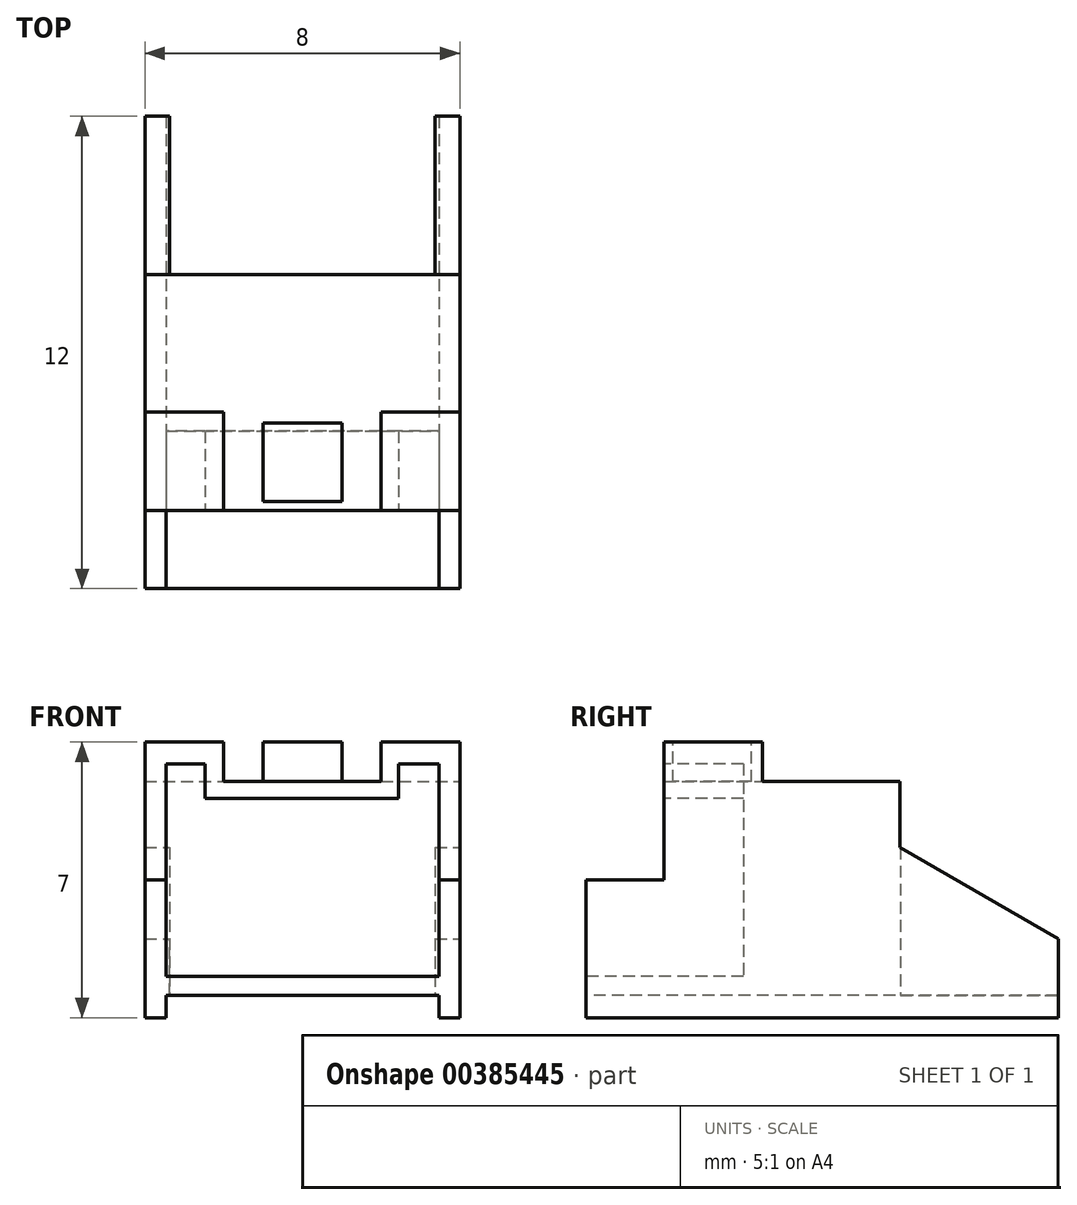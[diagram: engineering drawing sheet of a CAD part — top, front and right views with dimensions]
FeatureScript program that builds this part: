
annotation { "Feature Type Name" : "Feature", "Feature Type Description" : "" }
export const myFeature = defineFeature(function(context is Context, id is Id, definition is map)
    precondition{}
    {
        {
            var Q0;
            Q0=qCreatedBy(makeId("Right.planeOp"),FACE);
            var sketch = newSketch(context, id + "F0", { "sketchPlane" : qUnion([Q0])});
            skLineSegment(sketch, "E0", {"start": v(-5.54, 0) * mm, "end": v(6.46, 0) * mm});
            skLineSegment(sketch, "E1", {"start": v(6.46, 0) * mm, "end": v(6.46, 2) * mm});
            skLineSegment(sketch, "E2", {"start": v(6.46, 2) * mm, "end": v(2.45, 4.32) * mm});
            skLineSegment(sketch, "E3", {"start": v(2.45, 4.32) * mm, "end": v(2.45, 6) * mm});
            skLineSegment(sketch, "E4", {"start": v(2.45, 6) * mm, "end": v(0.95, 6) * mm});
            skLineSegment(sketch, "E5", {"start": v(0.95, 6) * mm, "end": v(0.95, 7) * mm});
            skLineSegment(sketch, "E6", {"start": v(0.95, 7) * mm, "end": v(-3.55, 7) * mm});
            skLineSegment(sketch, "E7", {"start": v(-3.55, 7) * mm, "end": v(-3.55, 3.5) * mm});
            skLineSegment(sketch, "E8", {"start": v(-3.55, 3.5) * mm, "end": v(-5.54, 3.5) * mm});
            skLineSegment(sketch, "E9", {"start": v(-5.54, 3.5) * mm, "end": v(-5.54, 0) * mm});
            skSolve(sketch);
        }
        {
            var Q0;
            Q0=makeQuery(id+"F0.imprint","IMPRINT",FACE,{"disambiguationData":[TD([[makeQuery(id+"F0.imprint","IMPRINT",EDGE,{"derivedFrom":sQuery(id+"F0.wireOp",EDGE,"E0")}),1.0]])]});
            extrude(context, id + "F1", {"entities" : qUnion([Q0]), "oppositeDirection" : true, "depth" : 8 * mm});
        }
        {
            var Q0;
            Q0=qCreatedBy(makeId("Top.planeOp"),FACE);
            var sketch = newSketch(context, id + "F2", { "sketchPlane" : qUnion([Q0])});
            skLineSegment(sketch, "E10.bottom", {"start": v(-0.63, 6.46) * mm, "end": v(-7.37, 6.46) * mm});
            skLineSegment(sketch, "E10.top", {"start": v(-0.63, 2.45) * mm, "end": v(-7.37, 2.45) * mm});
            skLineSegment(sketch, "E10.left", {"start": v(-0.63, 6.46) * mm, "end": v(-0.63, 2.45) * mm});
            skLineSegment(sketch, "E10.right", {"start": v(-7.37, 6.46) * mm, "end": v(-7.37, 2.45) * mm});
            skSolve(sketch);
        }
        {
            var Q0;
            Q0=qSketchRegion(id+"F2",true);
            extrude(context, id + "F3", {"entities" : qUnion([Q0]), "operationType" : NewBodyOperationType.REMOVE, "depth" : 25 * mm});
        }
        {
            var Q0;
            Q0=makeQuery(id+"F1.opExtrude","SWEPT_FACE",FACE,{"disambiguationData":[OSD([sQuery(id+"F0.wireOp",EDGE,"E6")])]});
            var sketch = newSketch(context, id + "F4", { "sketchPlane" : qUnion([Q0])});
            skLineSegment(sketch, "E11.bottom", {"start": v(-8, 0.95) * mm, "end": v(0, 0.95) * mm});
            skLineSegment(sketch, "E11.top", {"start": v(-8, -1.05) * mm, "end": v(0, -1.05) * mm});
            skLineSegment(sketch, "E11.left", {"start": v(-8, 0.95) * mm, "end": v(-8, -1.05) * mm});
            skLineSegment(sketch, "E11.right", {"start": v(0, 0.95) * mm, "end": v(0, -1.05) * mm});
            skLineSegment(sketch, "E12.bottom", {"start": v(-2, -3.55) * mm, "end": v(-6, -3.55) * mm});
            skLineSegment(sketch, "E12.top", {"start": v(-2, -1.05) * mm, "end": v(-6, -1.05) * mm});
            skLineSegment(sketch, "E12.left", {"start": v(-2, -3.55) * mm, "end": v(-2, -1.05) * mm});
            skLineSegment(sketch, "E12.right", {"start": v(-6, -3.55) * mm, "end": v(-6, -1.05) * mm});
            skLineSegment(sketch, "E13.bottom", {"start": v(-5, -1.33) * mm, "end": v(-3, -1.33) * mm});
            skLineSegment(sketch, "E13.top", {"start": v(-5, -3.33) * mm, "end": v(-3, -3.33) * mm});
            skLineSegment(sketch, "E13.left", {"start": v(-5, -1.33) * mm, "end": v(-5, -3.33) * mm});
            skLineSegment(sketch, "E13.right", {"start": v(-3, -1.33) * mm, "end": v(-3, -3.33) * mm});
            skSolve(sketch);
        }
        {
            var Q0;
            Q0=makeQuery(id+"F4.imprint","IMPRINT",FACE,{"disambiguationData":[TD([[makeQuery(id+"F4.imprint","IMPRINT",EDGE,{"derivedFrom":sQuery(id+"F4.wireOp",EDGE,"E11.bottom")}),-1.0]])]});
            var Q1;
            Q1=makeQuery(id+"F4.imprint","IMPRINT",FACE,{"disambiguationData":[TD([[makeQuery(id+"F4.imprint","IMPRINT",EDGE,{"derivedFrom":sQuery(id+"F4.wireOp",EDGE,"E12.bottom")}),1.0]])]});
            extrude(context, id + "F5", {"entities" : qUnion([Q0, Q1]), "operationType" : NewBodyOperationType.REMOVE, "oppositeDirection" : true, "depth" : 1 * mm});
        }
        {
            var Q0;
            Q0=makeQuery(id+"F1.opExtrude","SWEPT_FACE",FACE,{"disambiguationData":[OSD([sQuery(id+"F0.wireOp",EDGE,"E9")])]});
            var sketch = newSketch(context, id + "F6", { "sketchPlane" : qUnion([Q0])});
            skLineSegment(sketch, "E14.bottom", {"start": v(-7.47, 0) * mm, "end": v(-0.53, 0) * mm});
            skLineSegment(sketch, "E14.top", {"start": v(-7.47, 0.65) * mm, "end": v(-0.53, 0.65) * mm});
            skLineSegment(sketch, "E14.left", {"start": v(-7.47, 0) * mm, "end": v(-7.47, 0.65) * mm});
            skLineSegment(sketch, "E14.right", {"start": v(-0.53, 0) * mm, "end": v(-0.53, 0.65) * mm});
            skLineSegment(sketch, "E15", {"start": v(-7.47, 1.05) * mm, "end": v(-0.53, 1.05) * mm});
            skLineSegment(sketch, "E16", {"start": v(-0.53, 1.05) * mm, "end": v(-0.53, 6.45) * mm});
            skLineSegment(sketch, "E17", {"start": v(-0.53, 6.45) * mm, "end": v(-1.55, 6.45) * mm});
            skLineSegment(sketch, "E18", {"start": v(-1.55, 6.45) * mm, "end": v(-1.55, 5.58) * mm});
            skLineSegment(sketch, "E19", {"start": v(-1.55, 5.58) * mm, "end": v(-6.47, 5.58) * mm});
            skLineSegment(sketch, "E20", {"start": v(-6.47, 5.58) * mm, "end": v(-6.47, 6.45) * mm});
            skLineSegment(sketch, "E21", {"start": v(-6.47, 6.45) * mm, "end": v(-7.47, 6.45) * mm});
            skLineSegment(sketch, "E22", {"start": v(-7.47, 6.45) * mm, "end": v(-7.47, 1.05) * mm});
            skSolve(sketch);
        }
        {
            var Q0;
            {var subQ5=sQuery(id+"F6.wireOp",EDGE,"E17");Q0=makeQuery(id+"F6.imprint","IMPRINT",FACE,{"disambiguationData":[TD([[makeQuery(id+"F6.imprint","IMPRINT",EDGE,{"derivedFrom":subQ5}),1.0]])]});}
            var Q1;
            {var subQ0=sQuery(id+"F6.wireOp",EDGE,"E15");Q1=makeQuery(id+"F6.imprint","IMPRINT",FACE,{"disambiguationData":[TD([[makeQuery(id+"F6.imprint","IMPRINT",EDGE,{"derivedFrom":subQ0}),1.0]])]});}
            extrude(context, id + "F7", {"entities" : qUnion([Q0, Q1]), "operationType" : NewBodyOperationType.REMOVE, "oppositeDirection" : true, "depth" : 4 * mm});
        }
        {
            var Q0;
            Q0=makeQuery(id+"F1.opExtrude","SWEPT_FACE",FACE,{"disambiguationData":[OSD([sQuery(id+"F0.wireOp",EDGE,"E9")])]});
            var sketch = newSketch(context, id + "F8", { "sketchPlane" : qUnion([Q0])});
            skLineSegment(sketch, "E23.bottom", {"start": v(-7.47, 0) * mm, "end": v(-0.53, 0) * mm});
            skLineSegment(sketch, "E23.top", {"start": v(-7.47, 0.57) * mm, "end": v(-0.53, 0.57) * mm});
            skLineSegment(sketch, "E23.left", {"start": v(-7.47, 0) * mm, "end": v(-7.47, 0.57) * mm});
            skLineSegment(sketch, "E23.right", {"start": v(-0.53, 0) * mm, "end": v(-0.53, 0.57) * mm});
            skSolve(sketch);
        }
        {
            var Q0;
            Q0=makeQuery(id+"F8.imprint","IMPRINT",FACE,{"disambiguationData":[TD([[makeQuery(id+"F8.imprint","IMPRINT",EDGE,{"derivedFrom":sQuery(id+"F8.wireOp",EDGE,"E23.bottom")}),1.0]])]});
            extrude(context, id + "F9", {"entities" : qUnion([Q0]), "operationType" : NewBodyOperationType.REMOVE, "oppositeDirection" : true, "depth" : 25 * mm});
        }
    });
